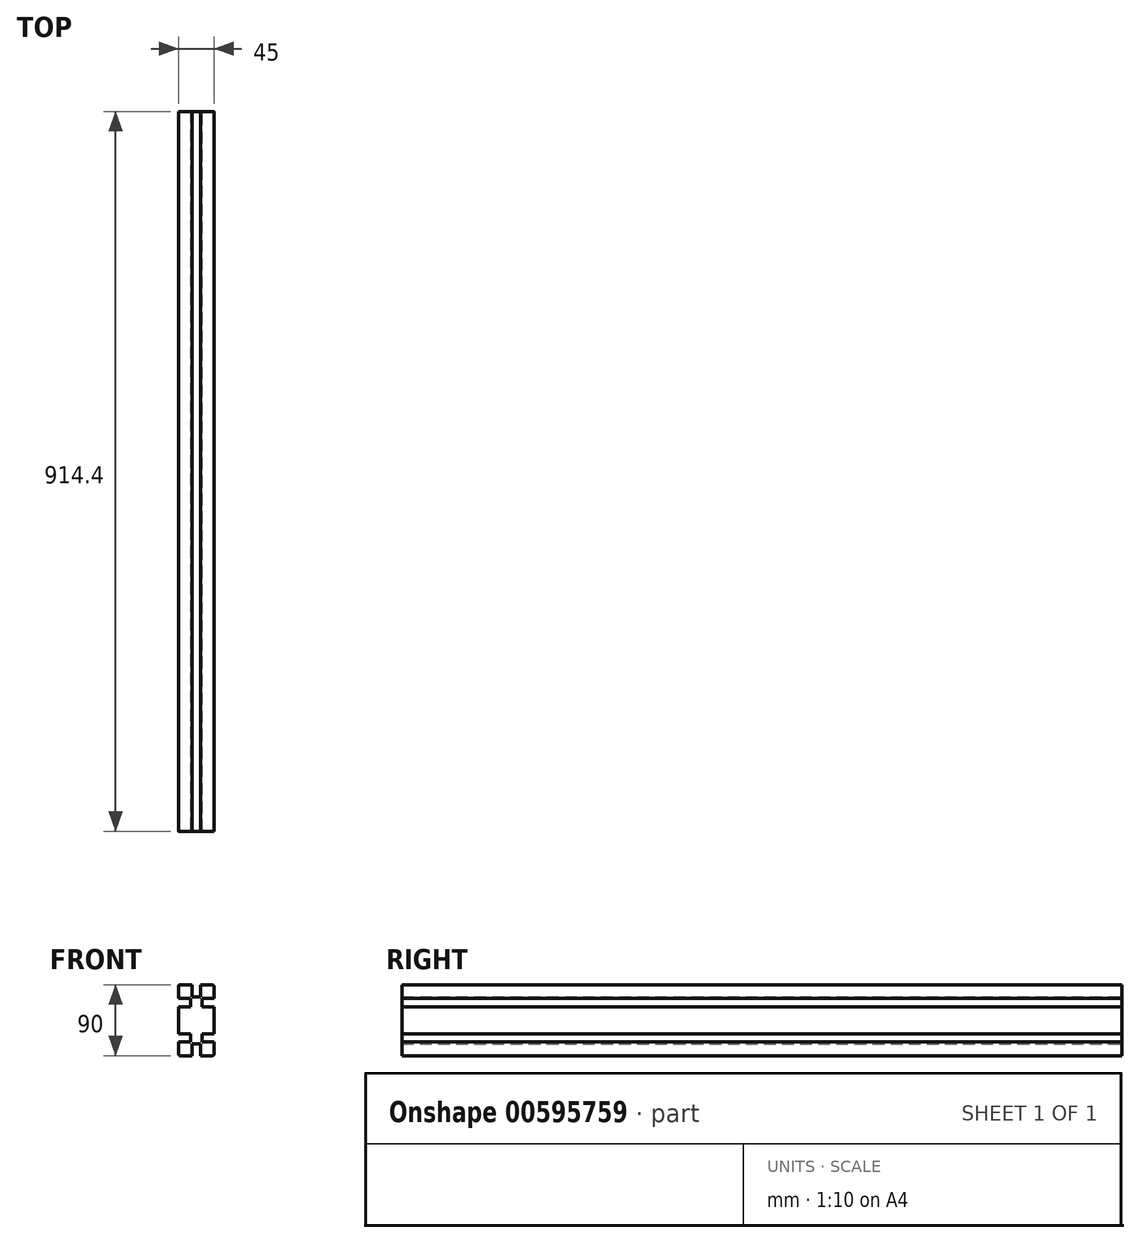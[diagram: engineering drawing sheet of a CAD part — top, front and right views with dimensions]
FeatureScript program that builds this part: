
annotation { "Feature Type Name" : "Feature", "Feature Type Description" : "" }
export const myFeature = defineFeature(function(context is Context, id is Id, definition is map)
    precondition{}
    {
        {
            var Q0;
            Q0=qCreatedBy(makeId("Front.planeOp"),FACE);
            var sketch = newSketch(context, id + "F0", { "sketchPlane" : qUnion([Q0])});
            skLineSegment(sketch, "E0.bottom", {"start": v(-22.5, 45) * mm, "end": v(22.5, 45) * mm});
            skLineSegment(sketch, "E0.top", {"start": v(-22.5, -45) * mm, "end": v(22.5, -45) * mm});
            skLineSegment(sketch, "E0.left", {"start": v(-22.5, 45) * mm, "end": v(-22.5, -45) * mm});
            skLineSegment(sketch, "E0.right", {"start": v(22.5, 45) * mm, "end": v(22.5, -45) * mm});
            skPoint(sketch, "E0.middle", {"position": v(0, 0) * mm});
            skSolve(sketch);
        }
        {
            var Q0;
            Q0=makeQuery(id+"F0.imprint","IMPRINT",FACE,{"disambiguationData":[TD([[makeQuery(id+"F0.imprint","IMPRINT",EDGE,{"derivedFrom":sQuery(id+"F0.wireOp",EDGE,"E0.bottom")}),-1.0]])]});
            extrude(context, id + "F1", {"entities" : qUnion([Q0]), "oppositeDirection" : true, "depth" : 914.4 * mm, "offsetDistance" : 25 * mm, "symmetric" : true});
        }
        {
            var Q0;
            Q0=makeQuery(id+"F1.opExtrude","SWEPT_FACE",FACE,{"disambiguationData":[OSD([sQuery(id+"F0.wireOp",EDGE,"E0.right")])]});
            var sketch = newSketch(context, id + "F2", { "sketchPlane" : qUnion([Q0])});
            skLineSegment(sketch, "E1.bottom", {"start": v(-457.2, 17.3) * mm, "end": v(457.2, 17.3) * mm});
            skLineSegment(sketch, "E1.top", {"start": v(-457.2, 27.7) * mm, "end": v(457.2, 27.7) * mm});
            skLineSegment(sketch, "E1.left", {"start": v(-457.2, 17.3) * mm, "end": v(-457.2, 27.7) * mm});
            skLineSegment(sketch, "E1.right", {"start": v(457.2, 17.3) * mm, "end": v(457.2, 27.7) * mm});
            skPoint(sketch, "E1.middle", {"position": v(0, 22.5) * mm});
            skLineSegment(sketch, "E2.bottom", {"start": v(-457.2, -17.3) * mm, "end": v(457.2, -17.3) * mm});
            skLineSegment(sketch, "E2.top", {"start": v(-457.2, -27.7) * mm, "end": v(457.2, -27.7) * mm});
            skLineSegment(sketch, "E2.left", {"start": v(-457.2, -17.3) * mm, "end": v(-457.2, -27.7) * mm});
            skLineSegment(sketch, "E2.right", {"start": v(457.2, -17.3) * mm, "end": v(457.2, -27.7) * mm});
            skPoint(sketch, "E2.middle", {"position": v(0, -22.5) * mm});
            skSolve(sketch);
        }
        {
            var Q0;
            Q0 = qSketchRegion(id + "F2", true);
            extrude(context, id + "F3", {"entities" : qUnion([Q0]), "operationType" : NewBodyOperationType.REMOVE, "oppositeDirection" : true, "depth" : 15 * mm, "offsetDistance" : 25 * mm});
        }
        {
            var Q0;
            Q0=makeQuery(id+"F1.opExtrude","SWEPT_FACE",FACE,{"disambiguationData":[OSD([sQuery(id+"F0.wireOp",EDGE,"E0.left")])]});
            var sketch = newSketch(context, id + "F4", { "sketchPlane" : qUnion([Q0])});
            skLineSegment(sketch, "E3.bottom", {"start": v(-457.2, 17.3) * mm, "end": v(457.2, 17.3) * mm});
            skLineSegment(sketch, "E3.top", {"start": v(-457.2, 27.7) * mm, "end": v(457.2, 27.7) * mm});
            skLineSegment(sketch, "E3.left", {"start": v(-457.2, 17.3) * mm, "end": v(-457.2, 27.7) * mm});
            skLineSegment(sketch, "E3.right", {"start": v(457.2, 17.3) * mm, "end": v(457.2, 27.7) * mm});
            skPoint(sketch, "E3.middle", {"position": v(0, 22.5) * mm});
            skLineSegment(sketch, "E4.bottom", {"start": v(-457.2, -27.7) * mm, "end": v(457.2, -27.7) * mm});
            skLineSegment(sketch, "E4.top", {"start": v(-457.2, -17.3) * mm, "end": v(457.2, -17.3) * mm});
            skLineSegment(sketch, "E4.left", {"start": v(-457.2, -27.7) * mm, "end": v(-457.2, -17.3) * mm});
            skLineSegment(sketch, "E4.right", {"start": v(457.2, -27.7) * mm, "end": v(457.2, -17.3) * mm});
            skPoint(sketch, "E4.middle", {"position": v(0, -22.5) * mm});
            skSolve(sketch);
        }
        {
            var Q0;
            Q0 = qSketchRegion(id + "F4", true);
            extrude(context, id + "F5", {"entities" : qUnion([Q0]), "operationType" : NewBodyOperationType.REMOVE, "oppositeDirection" : true, "depth" : 15 * mm, "offsetDistance" : 25 * mm});
        }
        {
            var Q0;
            Q0=makeQuery(id+"F1.opExtrude","SWEPT_FACE",FACE,{"disambiguationData":[OSD([sQuery(id+"F0.wireOp",EDGE,"E0.bottom")])]});
            var sketch = newSketch(context, id + "F6", { "sketchPlane" : qUnion([Q0])});
            skLineSegment(sketch, "E5.bottom", {"start": v(-5.2, -457.2) * mm, "end": v(5.2, -457.2) * mm});
            skLineSegment(sketch, "E5.top", {"start": v(-5.2, 457.2) * mm, "end": v(5.2, 457.2) * mm});
            skLineSegment(sketch, "E5.left", {"start": v(-5.2, -457.2) * mm, "end": v(-5.2, 457.2) * mm});
            skLineSegment(sketch, "E5.right", {"start": v(5.2, -457.2) * mm, "end": v(5.2, 457.2) * mm});
            skPoint(sketch, "E5.middle", {"position": v(0, 0) * mm});
            skSolve(sketch);
        }
        {
            var Q0;
            Q0=makeQuery(id+"F6.imprint","IMPRINT",FACE,{"disambiguationData":[TD([[makeQuery(id+"F6.imprint","IMPRINT",EDGE,{"derivedFrom":sQuery(id+"F6.wireOp",EDGE,"E5.bottom")}),1.0]])]});
            extrude(context, id + "F7", {"entities" : qUnion([Q0]), "operationType" : NewBodyOperationType.REMOVE, "oppositeDirection" : true, "depth" : 15 * mm, "offsetDistance" : 25 * mm});
        }
        {
            var Q0;
            Q0=makeQuery(id+"F1.opExtrude","SWEPT_FACE",FACE,{"disambiguationData":[OSD([sQuery(id+"F0.wireOp",EDGE,"E0.top")])]});
            var sketch = newSketch(context, id + "F8", { "sketchPlane" : qUnion([Q0])});
            skLineSegment(sketch, "E6.bottom", {"start": v(-5.2, 457.2) * mm, "end": v(5.2, 457.2) * mm});
            skLineSegment(sketch, "E6.top", {"start": v(-5.2, -457.2) * mm, "end": v(5.2, -457.2) * mm});
            skLineSegment(sketch, "E6.left", {"start": v(-5.2, 457.2) * mm, "end": v(-5.2, -457.2) * mm});
            skLineSegment(sketch, "E6.right", {"start": v(5.2, 457.2) * mm, "end": v(5.2, -457.2) * mm});
            skPoint(sketch, "E6.middle", {"position": v(0, 0) * mm});
            skSolve(sketch);
        }
        {
            var Q0;
            Q0=makeQuery(id+"F8.imprint","IMPRINT",FACE,{"disambiguationData":[TD([[makeQuery(id+"F8.imprint","IMPRINT",EDGE,{"derivedFrom":sQuery(id+"F8.wireOp",EDGE,"E6.bottom")}),-1.0]])]});
            extrude(context, id + "F9", {"entities" : qUnion([Q0]), "operationType" : NewBodyOperationType.REMOVE, "oppositeDirection" : true, "depth" : 15 * mm, "offsetDistance" : 25 * mm});
        }
        {
            var Q0;
            Q0=makeQuery(id+"F1.opExtrude","SWEPT_EDGE",EDGE,{"disambiguationData":[OSD([sQuery(id+"F0.wireOp",EDGE,"E0.bottom"),sQuery(id+"F0.wireOp",EDGE,"E0.right")])]});
            var Q1;
            Q1=makeQuery(id+"F1.opExtrude","SWEPT_EDGE",EDGE,{"disambiguationData":[OSD([sQuery(id+"F0.wireOp",EDGE,"E0.bottom"),sQuery(id+"F0.wireOp",EDGE,"E0.left")])]});
            var Q2;
            Q2=makeQuery(id+"F1.opExtrude","SWEPT_EDGE",EDGE,{"disambiguationData":[OSD([sQuery(id+"F0.wireOp",EDGE,"E0.top"),sQuery(id+"F0.wireOp",EDGE,"E0.right")])]});
            var Q3;
            Q3=makeQuery(id+"F1.opExtrude","SWEPT_EDGE",EDGE,{"disambiguationData":[OSD([sQuery(id+"F0.wireOp",EDGE,"E0.top"),sQuery(id+"F0.wireOp",EDGE,"E0.left")])]});
            fillet(context, id + "F10", {"entities" : qUnion([Q0, Q1, Q2, Q3]), "radius" : 2 * mm, "tangentPropagation" : true, "allowEdgeOverflow" : false});
        }
    });
